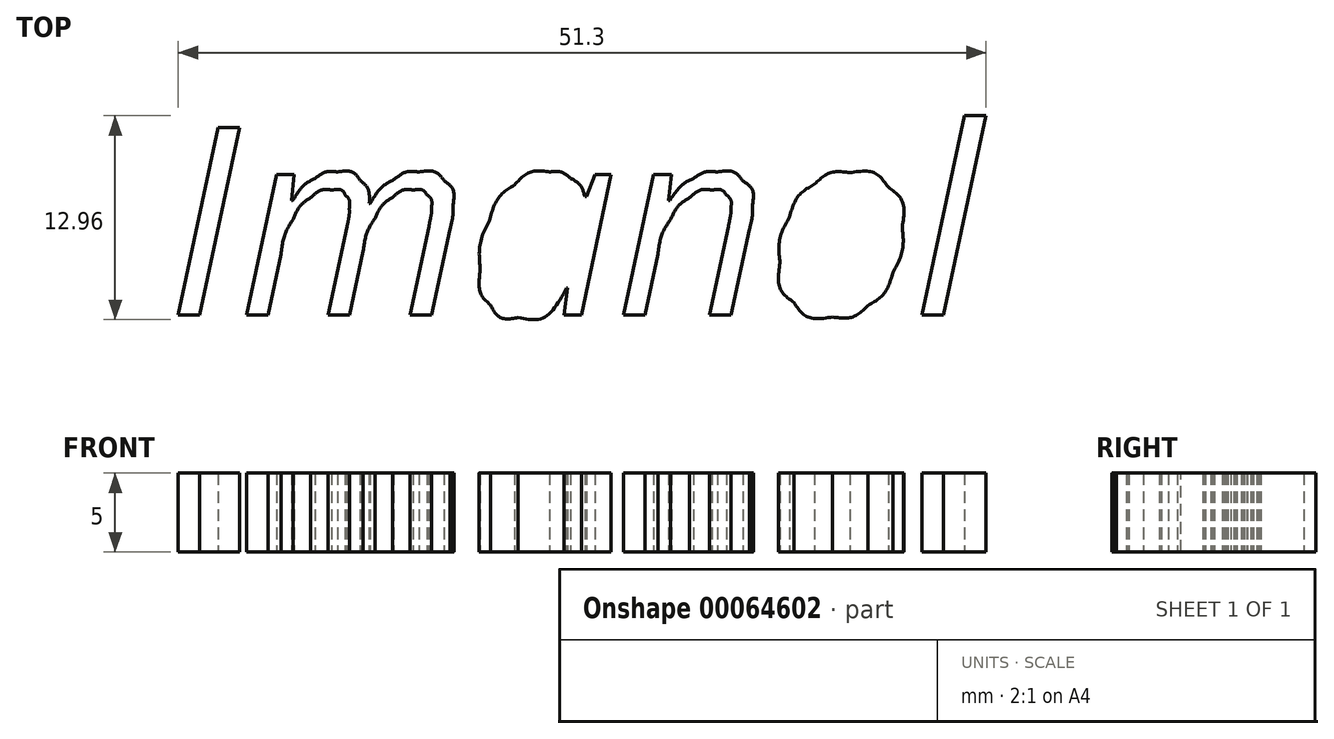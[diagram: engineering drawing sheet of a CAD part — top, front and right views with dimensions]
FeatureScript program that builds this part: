
annotation { "Feature Type Name" : "Feature", "Feature Type Description" : "" }
export const myFeature = defineFeature(function(context is Context, id is Id, definition is map)
    precondition{}
    {
        {
            var Q0;
            Q0=qCreatedBy(makeId("Top.planeOp"),FACE);
            var sketch = newSketch(context, id + "F0", { "sketchPlane" : qUnion([Q0])});
            skLineSegment(sketch, "E0.rect.bottom", {"start": v(30, 12.5) * mm, "end": v(-30, 12.5) * mm});
            skLineSegment(sketch, "E0.rect.top", {"start": v(30, -12.5) * mm, "end": v(-30, -12.5) * mm});
            skLineSegment(sketch, "E0.rect.left", {"start": v(30, 12.5) * mm, "end": v(30, -12.5) * mm});
            skPoint(sketch, "E0.rect.middle", {"position": v(0, 0) * mm});
            skArc(sketch, "E1", {"start": v(-30, 12.5) * mm, "mid": v(-42.5, 0) * mm, "end": v(-30, -12.5) * mm});
            skCircle(sketch, "E2", {"center": v(-35.34, 0) * mm, "radius": 2.5 * mm});
            skSolve(sketch);
        }
        {
            var Q0;
            Q0 = qSketchRegion(id + "F0", true);
            extrude(context, id + "F1", {"entities" : qUnion([Q0]), "depth" : 3 * mm});
        }
        {
            var Q0;
            Q0=makeQuery(id+"F1.opExtrude","CAP_FACE",FACE,{"disambiguationData":[OSD([sQuery(id+"F0.wireOp",EDGE,"E0.rect.bottom"),sQuery(id+"F0.wireOp",EDGE,"E0.rect.top"),sQuery(id+"F0.wireOp",EDGE,"E0.rect.left"),sQuery(id+"F0.wireOp",EDGE,"E1"),sQuery(id+"F0.wireOp",EDGE,"E2")])],"isStart":false});
            var sketch = newSketch(context, id + "F2", { "sketchPlane" : qUnion([Q0])});
            skLineSegment(sketch, "E3.0.0", {"start": v(-23.45, 7.78) * mm, "end": v(-25.98, -4.12) * mm});
            skLineSegment(sketch, "E3.0.1", {"start": v(-25.98, -4.12) * mm, "end": v(-24.61, -4.12) * mm});
            skLineSegment(sketch, "E3.0.2", {"start": v(-24.61, -4.12) * mm, "end": v(-22.08, 7.78) * mm});
            skLineSegment(sketch, "E3.0.3", {"start": v(-22.08, 7.78) * mm, "end": v(-23.45, 7.78) * mm});
            skLineSegment(sketch, "E4.0.0", {"start": v(-15.26, 1.51) * mm, "end": v(-16.47, -4.12) * mm});
            skLineSegment(sketch, "E4.0.1", {"start": v(-16.47, -4.12) * mm, "end": v(-15.1, -4.12) * mm});
            skLineSegment(sketch, "E4.0.2", {"start": v(-15.1, -4.12) * mm, "end": v(-14.23, -0.04) * mm});
            skFitSpline(sketch, "E4.0.3", {"points": [v(-14.23, -0.05) * mm, v(-13.98, 1.14) * mm, v(-13.5, 2) * mm]});
            skFitSpline(sketch, "E4.0.4", {"points": [v(-13.5, 2) * mm, v(-13, 2.87) * mm, v(-12.37, 3.34) * mm]});
            skFitSpline(sketch, "E4.0.5", {"points": [v(-12.37, 3.34) * mm, v(-11.72, 3.81) * mm, v(-11.06, 3.81) * mm]});
            skFitSpline(sketch, "E4.0.6", {"points": [v(-11.06, 3.81) * mm, v(-10.46, 3.81) * mm, v(-10.18, 3.5) * mm]});
            skFitSpline(sketch, "E4.0.7", {"points": [v(-10.18, 3.5) * mm, v(-9.9, 3.2) * mm, v(-9.9, 2.7) * mm]});
            skFitSpline(sketch, "E4.0.8", {"points": [v(-9.9, 2.7) * mm, v(-9.9, 2.36) * mm, v(-10.06, 1.51) * mm]});
            skLineSegment(sketch, "E4.0.9", {"start": v(-10.06, 1.51) * mm, "end": v(-11.27, -4.12) * mm});
            skLineSegment(sketch, "E4.0.10", {"start": v(-11.27, -4.12) * mm, "end": v(-9.88, -4.12) * mm});
            skLineSegment(sketch, "E4.0.11", {"start": v(-9.88, -4.12) * mm, "end": v(-8.71, 1.35) * mm});
            skFitSpline(sketch, "E4.0.12", {"points": [v(-8.71, 1.35) * mm, v(-8.53, 2.24) * mm, v(-8.53, 2.8) * mm]});
            skFitSpline(sketch, "E4.0.13", {"points": [v(-8.53, 2.8) * mm, v(-8.53, 3.85) * mm, v(-9.1, 4.4) * mm]});
            skFitSpline(sketch, "E4.0.14", {"points": [v(-9.1, 4.4) * mm, v(-9.66, 4.96) * mm, v(-10.7, 4.96) * mm]});
            skFitSpline(sketch, "E4.0.15", {"points": [v(-10.7, 4.96) * mm, v(-11.5, 4.96) * mm, v(-12.3, 4.47) * mm]});
            skFitSpline(sketch, "E4.0.16", {"points": [v(-12.3, 4.47) * mm, v(-13.08, 3.97) * mm, v(-13.78, 2.96) * mm]});
            skLineSegment(sketch, "E4.0.17", {"start": v(-13.78, 2.96) * mm, "end": v(-13.85, 2.96) * mm});
            skFitSpline(sketch, "E4.0.18", {"points": [v(-13.85, 2.96) * mm, v(-13.94, 3.9) * mm, v(-14.43, 4.43) * mm]});
            skFitSpline(sketch, "E4.0.19", {"points": [v(-14.43, 4.43) * mm, v(-14.93, 4.96) * mm, v(-15.85, 4.96) * mm]});
            skFitSpline(sketch, "E4.0.20", {"points": [v(-15.85, 4.96) * mm, v(-16.6, 4.96) * mm, v(-17.3, 4.54) * mm]});
            skFitSpline(sketch, "E4.0.21", {"points": [v(-17.3, 4.54) * mm, v(-18, 4.11) * mm, v(-18.71, 3.15) * mm]});
            skLineSegment(sketch, "E4.0.22", {"start": v(-18.71, 3.15) * mm, "end": v(-18.8, 3.15) * mm});
            skLineSegment(sketch, "E4.0.23", {"start": v(-18.8, 3.15) * mm, "end": v(-18.62, 4.8) * mm});
            skLineSegment(sketch, "E4.0.24", {"start": v(-18.62, 4.8) * mm, "end": v(-19.75, 4.8) * mm});
            skLineSegment(sketch, "E4.0.25", {"start": v(-19.75, 4.8) * mm, "end": v(-21.65, -4.12) * mm});
            skLineSegment(sketch, "E4.0.26", {"start": v(-21.65, -4.12) * mm, "end": v(-20.29, -4.12) * mm});
            skLineSegment(sketch, "E4.0.27", {"start": v(-20.29, -4.12) * mm, "end": v(-19.46, -0.26) * mm});
            skFitSpline(sketch, "E4.0.28", {"points": [v(-19.46, -0.26) * mm, v(-19.2, 1.02) * mm, v(-18.7, 1.93) * mm]});
            skFitSpline(sketch, "E4.0.29", {"points": [v(-18.7, 1.93) * mm, v(-18.21, 2.84) * mm, v(-17.56, 3.32) * mm]});
            skFitSpline(sketch, "E4.0.30", {"points": [v(-17.56, 3.32) * mm, v(-16.92, 3.81) * mm, v(-16.23, 3.81) * mm]});
            skFitSpline(sketch, "E4.0.31", {"points": [v(-16.23, 3.81) * mm, v(-15.62, 3.81) * mm, v(-15.37, 3.5) * mm]});
            skFitSpline(sketch, "E4.0.32", {"points": [v(-15.37, 3.5) * mm, v(-15.12, 3.18) * mm, v(-15.12, 2.6) * mm]});
            skFitSpline(sketch, "E4.0.33", {"points": [v(-15.12, 2.6) * mm, v(-15.12, 2.27) * mm, v(-15.26, 1.51) * mm]});
            skFitSpline(sketch, "E5.0.0", {"points": [v(-1.06, 4.56) * mm, v(-1.65, 4.96) * mm, v(-2.4, 4.96) * mm]});
            skFitSpline(sketch, "E5.0.1", {"points": [v(-2.4, 4.96) * mm, v(-3.61, 4.96) * mm, v(-4.63, 4.14) * mm]});
            skFitSpline(sketch, "E5.0.2", {"points": [v(-4.63, 4.14) * mm, v(-5.64, 3.32) * mm, v(-6.22, 1.87) * mm]});
            skFitSpline(sketch, "E5.0.3", {"points": [v(-6.22, 1.87) * mm, v(-6.8, 0.42) * mm, v(-6.8, -1.27) * mm]});
            skFitSpline(sketch, "E5.0.4", {"points": [v(-6.8, -1.27) * mm, v(-6.8, -2.67) * mm, v(-6.16, -3.48) * mm]});
            skFitSpline(sketch, "E5.0.5", {"points": [v(-6.16, -3.48) * mm, v(-5.51, -4.29) * mm, v(-4.38, -4.29) * mm]});
            skFitSpline(sketch, "E5.0.6", {"points": [v(-4.38, -4.29) * mm, v(-2.77, -4.29) * mm, v(-1.31, -2.42) * mm]});
            skLineSegment(sketch, "E5.0.7", {"start": v(-1.31, -2.42) * mm, "end": v(-1.25, -2.42) * mm});
            skLineSegment(sketch, "E5.0.8", {"start": v(-1.25, -2.42) * mm, "end": v(-1.46, -4.12) * mm});
            skLineSegment(sketch, "E5.0.9", {"start": v(-1.46, -4.12) * mm, "end": v(-0.38, -4.12) * mm});
            skLineSegment(sketch, "E5.0.10", {"start": v(-0.38, -4.12) * mm, "end": v(1.52, 4.8) * mm});
            skLineSegment(sketch, "E5.0.11", {"start": v(1.52, 4.8) * mm, "end": v(0.48, 4.8) * mm});
            skLineSegment(sketch, "E5.0.12", {"start": v(0.48, 4.8) * mm, "end": v(-0.06, 3.4) * mm});
            skLineSegment(sketch, "E5.0.13", {"start": v(-0.06, 3.4) * mm, "end": v(-0.15, 3.4) * mm});
            skFitSpline(sketch, "E5.0.14", {"points": [v(-0.15, 3.4) * mm, v(-0.48, 4.15) * mm, v(-1.06, 4.56) * mm]});
            skLineSegment(sketch, "E6.0.0", {"start": v(8.96, 1.51) * mm, "end": v(7.75, -4.12) * mm});
            skLineSegment(sketch, "E6.0.1", {"start": v(7.75, -4.12) * mm, "end": v(9.13, -4.12) * mm});
            skLineSegment(sketch, "E6.0.2", {"start": v(9.13, -4.12) * mm, "end": v(10.3, 1.35) * mm});
            skFitSpline(sketch, "E6.0.3", {"points": [v(10.3, 1.35) * mm, v(10.49, 2.17) * mm, v(10.49, 2.81) * mm]});
            skFitSpline(sketch, "E6.0.4", {"points": [v(10.49, 2.81) * mm, v(10.49, 3.83) * mm, v(9.89, 4.4) * mm]});
            skFitSpline(sketch, "E6.0.5", {"points": [v(9.89, 4.4) * mm, v(9.29, 4.96) * mm, v(8.26, 4.96) * mm]});
            skFitSpline(sketch, "E6.0.6", {"points": [v(8.26, 4.96) * mm, v(7.47, 4.96) * mm, v(6.75, 4.55) * mm]});
            skFitSpline(sketch, "E6.0.7", {"points": [v(6.75, 4.55) * mm, v(6.02, 4.14) * mm, v(5.24, 3.15) * mm]});
            skLineSegment(sketch, "E6.0.8", {"start": v(5.24, 3.15) * mm, "end": v(5.15, 3.15) * mm});
            skLineSegment(sketch, "E6.0.9", {"start": v(5.15, 3.15) * mm, "end": v(5.33, 4.8) * mm});
            skLineSegment(sketch, "E6.0.10", {"start": v(5.33, 4.8) * mm, "end": v(4.2, 4.8) * mm});
            skLineSegment(sketch, "E6.0.11", {"start": v(4.2, 4.8) * mm, "end": v(2.3, -4.12) * mm});
            skLineSegment(sketch, "E6.0.12", {"start": v(2.3, -4.12) * mm, "end": v(3.66, -4.12) * mm});
            skLineSegment(sketch, "E6.0.13", {"start": v(3.66, -4.12) * mm, "end": v(4.49, -0.26) * mm});
            skFitSpline(sketch, "E6.0.14", {"points": [v(4.49, -0.26) * mm, v(4.76, 1.03) * mm, v(5.28, 1.93) * mm]});
            skFitSpline(sketch, "E6.0.15", {"points": [v(5.28, 1.93) * mm, v(5.8, 2.84) * mm, v(6.5, 3.32) * mm]});
            skFitSpline(sketch, "E6.0.16", {"points": [v(6.5, 3.32) * mm, v(7.18, 3.81) * mm, v(7.9, 3.81) * mm]});
            skFitSpline(sketch, "E6.0.17", {"points": [v(7.9, 3.81) * mm, v(8.54, 3.81) * mm, v(8.83, 3.5) * mm]});
            skFitSpline(sketch, "E6.0.18", {"points": [v(8.83, 3.5) * mm, v(9.12, 3.2) * mm, v(9.12, 2.68) * mm]});
            skFitSpline(sketch, "E6.0.19", {"points": [v(9.12, 2.68) * mm, v(9.12, 2.36) * mm, v(8.96, 1.51) * mm]});
            skFitSpline(sketch, "E7.0.0", {"points": [v(19.11, 4) * mm, v(18.22, 4.91) * mm, v(16.67, 4.91) * mm]});
            skFitSpline(sketch, "E7.0.1", {"points": [v(16.67, 4.91) * mm, v(15.44, 4.91) * mm, v(14.43, 4.18) * mm]});
            skFitSpline(sketch, "E7.0.2", {"points": [v(14.43, 4.18) * mm, v(13.43, 3.45) * mm, v(12.83, 2.1) * mm]});
            skFitSpline(sketch, "E7.0.3", {"points": [v(12.83, 2.1) * mm, v(12.24, 0.73) * mm, v(12.24, -0.82) * mm]});
            skFitSpline(sketch, "E7.0.4", {"points": [v(12.24, -0.82) * mm, v(12.24, -2.41) * mm, v(13.12, -3.33) * mm]});
            skFitSpline(sketch, "E7.0.5", {"points": [v(13.12, -3.33) * mm, v(14.01, -4.25) * mm, v(15.57, -4.25) * mm]});
            skFitSpline(sketch, "E7.0.6", {"points": [v(15.57, -4.25) * mm, v(16.83, -4.25) * mm, v(17.84, -3.51) * mm]});
            skFitSpline(sketch, "E7.0.7", {"points": [v(17.84, -3.51) * mm, v(18.84, -2.77) * mm, v(19.42, -1.41) * mm]});
            skFitSpline(sketch, "E7.0.8", {"points": [v(19.42, -1.41) * mm, v(20, -0.05) * mm, v(20, 1.48) * mm]});
            skFitSpline(sketch, "E7.0.9", {"points": [v(20, 1.48) * mm, v(20, 3.08) * mm, v(19.11, 4) * mm]});
            skLineSegment(sketch, "E8.0.0", {"start": v(21.25, -4.12) * mm, "end": v(22.62, -4.12) * mm});
            skLineSegment(sketch, "E8.0.1", {"start": v(22.62, -4.12) * mm, "end": v(25.32, 8.54) * mm});
            skLineSegment(sketch, "E8.0.2", {"start": v(25.32, 8.54) * mm, "end": v(23.96, 8.54) * mm});
            skLineSegment(sketch, "E8.0.3", {"start": v(23.96, 8.54) * mm, "end": v(21.25, -4.12) * mm});
            skLineSegment(sketch, "E9.rect.bottom", {"start": v(42.93, 26.44) * mm, "end": v(-52.19, 26.44) * mm});
            skLineSegment(sketch, "E9.rect.top", {"start": v(42.93, -31.29) * mm, "end": v(-52.19, -31.29) * mm});
            skLineSegment(sketch, "E9.rect.left", {"start": v(42.93, 26.44) * mm, "end": v(42.93, -31.29) * mm});
            skLineSegment(sketch, "E9.rect.right", {"start": v(-52.19, 26.44) * mm, "end": v(-52.19, -31.29) * mm});
            skPoint(sketch, "E9.rect.middle", {"position": v(-4.63, -2.42) * mm});
            skSolve(sketch);
        }
        {
            var Q0;
            Q0=makeQuery(id+"F2.imprint","IMPRINT",FACE,{"disambiguationData":[TD([[makeQuery(id+"F2.imprint","IMPRINT",EDGE,{"derivedFrom":sQuery(id+"F2.wireOp",EDGE,"E3.0.0")}),1.0]])]});
            var Q1;
            Q1=makeQuery(id+"F2.imprint","IMPRINT",FACE,{"disambiguationData":[TD([[makeQuery(id+"F2.imprint","IMPRINT",EDGE,{"derivedFrom":sQuery(id+"F2.wireOp",EDGE,"E4.0.0")}),1.0]])]});
            var Q2;
            Q2=makeQuery(id+"F2.imprint","IMPRINT",FACE,{"disambiguationData":[TD([[makeQuery(id+"F2.imprint","IMPRINT",EDGE,{"derivedFrom":sQuery(id+"F2.wireOp",EDGE,"E5.0.0")}),1.0]])]});
            var Q3;
            Q3=makeQuery(id+"F2.imprint","IMPRINT",FACE,{"disambiguationData":[TD([[makeQuery(id+"F2.imprint","IMPRINT",EDGE,{"derivedFrom":sQuery(id+"F2.wireOp",EDGE,"E6.0.0")}),1.0]])]});
            var Q4;
            Q4=makeQuery(id+"F2.imprint","IMPRINT",FACE,{"disambiguationData":[TD([[makeQuery(id+"F2.imprint","IMPRINT",EDGE,{"derivedFrom":sQuery(id+"F2.wireOp",EDGE,"E7.0.0")}),1.0]])]});
            var Q5;
            Q5=makeQuery(id+"F2.imprint","IMPRINT",FACE,{"disambiguationData":[TD([[makeQuery(id+"F2.imprint","IMPRINT",EDGE,{"derivedFrom":sQuery(id+"F2.wireOp",EDGE,"E8.0.0")}),1.0]])]});
            extrude(context, id + "F3", {"entities" : qUnion([Q0, Q1, Q2, Q3, Q4, Q5]), "operationType" : NewBodyOperationType.REMOVE, "oppositeDirection" : true, "depth" : 2 * mm});
        }
        {
            var Q0;
            Q0 = qSketchRegion(id + "F2", true);
            extrude(context, id + "F4", {"entities" : qUnion([Q0]), "operationType" : NewBodyOperationType.REMOVE, "oppositeDirection" : true, "depth" : 25 * mm});
        }
        {
            var Q0;
            Q0=makeQuery(id+"F3.boolean.opBoolean","COPY",FACE,{"derivedFrom":makeQuery(id+"F3.opExtrude","CAP_FACE",FACE,{"disambiguationData":[OSD([sQuery(id+"F2.wireOp",EDGE,"E5.0.0"),sQuery(id+"F2.wireOp",EDGE,"E5.0.1"),sQuery(id+"F2.wireOp",EDGE,"E5.0.2"),sQuery(id+"F2.wireOp",EDGE,"E5.0.3"),sQuery(id+"F2.wireOp",EDGE,"E5.0.4"),sQuery(id+"F2.wireOp",EDGE,"E5.0.5"),sQuery(id+"F2.wireOp",EDGE,"E5.0.6"),sQuery(id+"F2.wireOp",EDGE,"E5.0.7"),sQuery(id+"F2.wireOp",EDGE,"E5.0.8"),sQuery(id+"F2.wireOp",EDGE,"E5.0.9"),sQuery(id+"F2.wireOp",EDGE,"E5.0.10"),sQuery(id+"F2.wireOp",EDGE,"E5.0.11"),sQuery(id+"F2.wireOp",EDGE,"E5.0.12"),sQuery(id+"F2.wireOp",EDGE,"E5.0.13"),sQuery(id+"F2.wireOp",EDGE,"E5.0.14")])],"isStart":false})});
            var sketch = newSketch(context, id + "F5", { "sketchPlane" : qUnion([Q0])});
            skLineSegment(sketch, "E10.0.0", {"start": v(-22.08, 7.78) * mm, "end": v(-23.45, 7.78) * mm});
            skLineSegment(sketch, "E10.0.1", {"start": v(-23.45, 7.78) * mm, "end": v(-25.98, -4.12) * mm});
            skLineSegment(sketch, "E10.0.2", {"start": v(-25.98, -4.12) * mm, "end": v(-24.61, -4.12) * mm});
            skLineSegment(sketch, "E10.0.3", {"start": v(-24.61, -4.12) * mm, "end": v(-22.08, 7.78) * mm});
            skFitSpline(sketch, "E11.0.0", {"points": [v(-15.12, 2.6) * mm, v(-15.12, 2.27) * mm, v(-15.26, 1.51) * mm]});
            skLineSegment(sketch, "E11.0.1", {"start": v(-15.26, 1.51) * mm, "end": v(-16.47, -4.12) * mm});
            skLineSegment(sketch, "E11.0.2", {"start": v(-16.47, -4.12) * mm, "end": v(-15.1, -4.12) * mm});
            skLineSegment(sketch, "E11.0.3", {"start": v(-15.1, -4.12) * mm, "end": v(-14.23, -0.04) * mm});
            skFitSpline(sketch, "E11.0.4", {"points": [v(-14.23, -0.05) * mm, v(-13.98, 1.14) * mm, v(-13.5, 2) * mm]});
            skFitSpline(sketch, "E11.0.5", {"points": [v(-13.5, 2) * mm, v(-13, 2.87) * mm, v(-12.37, 3.34) * mm]});
            skFitSpline(sketch, "E11.0.6", {"points": [v(-12.37, 3.34) * mm, v(-11.72, 3.81) * mm, v(-11.06, 3.81) * mm]});
            skFitSpline(sketch, "E11.0.7", {"points": [v(-11.06, 3.81) * mm, v(-10.46, 3.81) * mm, v(-10.18, 3.5) * mm]});
            skFitSpline(sketch, "E11.0.8", {"points": [v(-10.18, 3.5) * mm, v(-9.9, 3.2) * mm, v(-9.9, 2.7) * mm]});
            skFitSpline(sketch, "E11.0.9", {"points": [v(-9.9, 2.7) * mm, v(-9.9, 2.36) * mm, v(-10.06, 1.51) * mm]});
            skLineSegment(sketch, "E11.0.10", {"start": v(-10.06, 1.51) * mm, "end": v(-11.27, -4.12) * mm});
            skLineSegment(sketch, "E11.0.11", {"start": v(-11.27, -4.12) * mm, "end": v(-9.88, -4.12) * mm});
            skLineSegment(sketch, "E11.0.12", {"start": v(-9.88, -4.12) * mm, "end": v(-8.71, 1.35) * mm});
            skFitSpline(sketch, "E11.0.13", {"points": [v(-8.71, 1.35) * mm, v(-8.53, 2.24) * mm, v(-8.53, 2.8) * mm]});
            skFitSpline(sketch, "E11.0.14", {"points": [v(-8.53, 2.8) * mm, v(-8.53, 3.85) * mm, v(-9.1, 4.4) * mm]});
            skFitSpline(sketch, "E11.0.15", {"points": [v(-9.1, 4.4) * mm, v(-9.66, 4.96) * mm, v(-10.7, 4.96) * mm]});
            skFitSpline(sketch, "E11.0.16", {"points": [v(-10.7, 4.96) * mm, v(-11.5, 4.96) * mm, v(-12.3, 4.47) * mm]});
            skFitSpline(sketch, "E11.0.17", {"points": [v(-12.3, 4.47) * mm, v(-13.08, 3.97) * mm, v(-13.78, 2.96) * mm]});
            skLineSegment(sketch, "E11.0.18", {"start": v(-13.78, 2.96) * mm, "end": v(-13.85, 2.96) * mm});
            skFitSpline(sketch, "E11.0.19", {"points": [v(-13.85, 2.96) * mm, v(-13.94, 3.9) * mm, v(-14.43, 4.43) * mm]});
            skFitSpline(sketch, "E11.0.20", {"points": [v(-14.43, 4.43) * mm, v(-14.93, 4.96) * mm, v(-15.85, 4.96) * mm]});
            skFitSpline(sketch, "E11.0.21", {"points": [v(-15.85, 4.96) * mm, v(-16.6, 4.96) * mm, v(-17.3, 4.54) * mm]});
            skFitSpline(sketch, "E11.0.22", {"points": [v(-17.3, 4.54) * mm, v(-18, 4.11) * mm, v(-18.71, 3.15) * mm]});
            skLineSegment(sketch, "E11.0.23", {"start": v(-18.71, 3.15) * mm, "end": v(-18.8, 3.15) * mm});
            skLineSegment(sketch, "E11.0.24", {"start": v(-18.8, 3.15) * mm, "end": v(-18.62, 4.8) * mm});
            skLineSegment(sketch, "E11.0.25", {"start": v(-18.62, 4.8) * mm, "end": v(-19.75, 4.8) * mm});
            skLineSegment(sketch, "E11.0.26", {"start": v(-19.75, 4.8) * mm, "end": v(-21.65, -4.12) * mm});
            skLineSegment(sketch, "E11.0.27", {"start": v(-21.65, -4.12) * mm, "end": v(-20.29, -4.12) * mm});
            skLineSegment(sketch, "E11.0.28", {"start": v(-20.29, -4.12) * mm, "end": v(-19.46, -0.26) * mm});
            skFitSpline(sketch, "E11.0.29", {"points": [v(-19.46, -0.26) * mm, v(-19.2, 1.02) * mm, v(-18.7, 1.93) * mm]});
            skFitSpline(sketch, "E11.0.30", {"points": [v(-18.7, 1.93) * mm, v(-18.21, 2.84) * mm, v(-17.56, 3.32) * mm]});
            skFitSpline(sketch, "E11.0.31", {"points": [v(-17.56, 3.32) * mm, v(-16.92, 3.81) * mm, v(-16.23, 3.81) * mm]});
            skFitSpline(sketch, "E11.0.32", {"points": [v(-16.23, 3.81) * mm, v(-15.62, 3.81) * mm, v(-15.37, 3.5) * mm]});
            skFitSpline(sketch, "E11.0.33", {"points": [v(-15.37, 3.5) * mm, v(-15.12, 3.18) * mm, v(-15.12, 2.6) * mm]});
            skFitSpline(sketch, "E12.0.0", {"points": [v(-0.15, 3.4) * mm, v(-0.48, 4.15) * mm, v(-1.06, 4.56) * mm]});
            skFitSpline(sketch, "E12.0.1", {"points": [v(-1.06, 4.56) * mm, v(-1.65, 4.96) * mm, v(-2.4, 4.96) * mm]});
            skFitSpline(sketch, "E12.0.2", {"points": [v(-2.4, 4.96) * mm, v(-3.61, 4.96) * mm, v(-4.63, 4.14) * mm]});
            skFitSpline(sketch, "E12.0.3", {"points": [v(-4.63, 4.14) * mm, v(-5.64, 3.32) * mm, v(-6.22, 1.87) * mm]});
            skFitSpline(sketch, "E12.0.4", {"points": [v(-6.22, 1.87) * mm, v(-6.8, 0.42) * mm, v(-6.8, -1.27) * mm]});
            skFitSpline(sketch, "E12.0.5", {"points": [v(-6.8, -1.27) * mm, v(-6.8, -2.67) * mm, v(-6.16, -3.48) * mm]});
            skFitSpline(sketch, "E12.0.6", {"points": [v(-6.16, -3.48) * mm, v(-5.51, -4.29) * mm, v(-4.38, -4.29) * mm]});
            skFitSpline(sketch, "E12.0.7", {"points": [v(-4.38, -4.29) * mm, v(-2.77, -4.29) * mm, v(-1.31, -2.42) * mm]});
            skLineSegment(sketch, "E12.0.8", {"start": v(-1.31, -2.42) * mm, "end": v(-1.25, -2.42) * mm});
            skLineSegment(sketch, "E12.0.9", {"start": v(-1.25, -2.42) * mm, "end": v(-1.46, -4.12) * mm});
            skLineSegment(sketch, "E12.0.10", {"start": v(-1.46, -4.12) * mm, "end": v(-0.38, -4.12) * mm});
            skLineSegment(sketch, "E12.0.11", {"start": v(-0.38, -4.12) * mm, "end": v(1.52, 4.8) * mm});
            skLineSegment(sketch, "E12.0.12", {"start": v(1.52, 4.8) * mm, "end": v(0.48, 4.8) * mm});
            skLineSegment(sketch, "E12.0.13", {"start": v(0.48, 4.8) * mm, "end": v(-0.06, 3.4) * mm});
            skLineSegment(sketch, "E12.0.14", {"start": v(-0.06, 3.4) * mm, "end": v(-0.15, 3.4) * mm});
            skLineSegment(sketch, "E13.0", {"start": v(4.2, 4.8) * mm, "end": v(2.3, -4.12) * mm});
            skFitSpline(sketch, "E14.0", {"points": [v(4.49, -0.26) * mm, v(4.76, 1.03) * mm, v(5.28, 1.93) * mm]});
            skFitSpline(sketch, "E15.0.0", {"points": [v(20, 1.48) * mm, v(20, 3.08) * mm, v(19.11, 4) * mm]});
            skFitSpline(sketch, "E15.0.1", {"points": [v(19.11, 4) * mm, v(18.22, 4.91) * mm, v(16.67, 4.91) * mm]});
            skFitSpline(sketch, "E15.0.2", {"points": [v(16.67, 4.91) * mm, v(15.44, 4.91) * mm, v(14.43, 4.18) * mm]});
            skFitSpline(sketch, "E15.0.3", {"points": [v(14.43, 4.18) * mm, v(13.43, 3.45) * mm, v(12.83, 2.1) * mm]});
            skFitSpline(sketch, "E15.0.4", {"points": [v(12.83, 2.1) * mm, v(12.24, 0.73) * mm, v(12.24, -0.82) * mm]});
            skFitSpline(sketch, "E15.0.5", {"points": [v(12.24, -0.82) * mm, v(12.24, -2.41) * mm, v(13.12, -3.33) * mm]});
            skFitSpline(sketch, "E15.0.6", {"points": [v(13.12, -3.33) * mm, v(14.01, -4.25) * mm, v(15.57, -4.25) * mm]});
            skFitSpline(sketch, "E15.0.7", {"points": [v(15.57, -4.25) * mm, v(16.83, -4.25) * mm, v(17.84, -3.51) * mm]});
            skFitSpline(sketch, "E15.0.8", {"points": [v(17.84, -3.51) * mm, v(18.84, -2.77) * mm, v(19.42, -1.41) * mm]});
            skFitSpline(sketch, "E15.0.9", {"points": [v(19.42, -1.41) * mm, v(20, -0.05) * mm, v(20, 1.48) * mm]});
            skFitSpline(sketch, "E16.0.0", {"points": [v(9.12, 2.68) * mm, v(9.12, 2.36) * mm, v(8.96, 1.51) * mm]});
            skLineSegment(sketch, "E16.0.1", {"start": v(8.96, 1.51) * mm, "end": v(7.75, -4.12) * mm});
            skLineSegment(sketch, "E16.0.2", {"start": v(7.75, -4.12) * mm, "end": v(9.13, -4.12) * mm});
            skLineSegment(sketch, "E16.0.3", {"start": v(9.13, -4.12) * mm, "end": v(10.3, 1.35) * mm});
            skFitSpline(sketch, "E16.0.4", {"points": [v(10.3, 1.35) * mm, v(10.49, 2.17) * mm, v(10.49, 2.81) * mm]});
            skFitSpline(sketch, "E16.0.5", {"points": [v(10.49, 2.81) * mm, v(10.49, 3.83) * mm, v(9.89, 4.4) * mm]});
            skFitSpline(sketch, "E16.0.6", {"points": [v(9.89, 4.4) * mm, v(9.29, 4.96) * mm, v(8.26, 4.96) * mm]});
            skFitSpline(sketch, "E16.0.7", {"points": [v(8.26, 4.96) * mm, v(7.47, 4.96) * mm, v(6.75, 4.55) * mm]});
            skFitSpline(sketch, "E16.0.8", {"points": [v(6.75, 4.55) * mm, v(6.02, 4.14) * mm, v(5.24, 3.15) * mm]});
            skLineSegment(sketch, "E16.0.9", {"start": v(5.24, 3.15) * mm, "end": v(5.15, 3.15) * mm});
            skLineSegment(sketch, "E16.0.10", {"start": v(5.15, 3.15) * mm, "end": v(5.33, 4.8) * mm});
            skLineSegment(sketch, "E16.0.11", {"start": v(5.33, 4.8) * mm, "end": v(4.2, 4.8) * mm});
            skLineSegment(sketch, "E16.0.13", {"start": v(2.3, -4.12) * mm, "end": v(3.66, -4.12) * mm});
            skLineSegment(sketch, "E16.0.14", {"start": v(3.66, -4.12) * mm, "end": v(4.49, -0.26) * mm});
            skFitSpline(sketch, "E16.0.15", {"points": [v(4.49, -0.26) * mm, v(4.76, 1.03) * mm, v(5.28, 1.93) * mm]});
            skFitSpline(sketch, "E16.0.16", {"points": [v(5.28, 1.93) * mm, v(5.8, 2.84) * mm, v(6.5, 3.32) * mm]});
            skFitSpline(sketch, "E16.0.17", {"points": [v(6.5, 3.32) * mm, v(7.18, 3.81) * mm, v(7.9, 3.81) * mm]});
            skFitSpline(sketch, "E16.0.18", {"points": [v(7.9, 3.81) * mm, v(8.54, 3.81) * mm, v(8.83, 3.5) * mm]});
            skFitSpline(sketch, "E16.0.19", {"points": [v(8.83, 3.5) * mm, v(9.12, 3.2) * mm, v(9.12, 2.68) * mm]});
            skLineSegment(sketch, "E17.0.0", {"start": v(23.96, 8.54) * mm, "end": v(21.25, -4.12) * mm});
            skLineSegment(sketch, "E17.0.1", {"start": v(21.25, -4.12) * mm, "end": v(22.62, -4.12) * mm});
            skLineSegment(sketch, "E17.0.2", {"start": v(22.62, -4.12) * mm, "end": v(25.32, 8.54) * mm});
            skLineSegment(sketch, "E17.0.3", {"start": v(25.32, 8.54) * mm, "end": v(23.96, 8.54) * mm});
            skSolve(sketch);
        }
        {
            var Q0;
            Q0 = qSketchRegion(id + "F5", true);
            extrude(context, id + "F6", {"entities" : qUnion([Q0]), "depth" : 5 * mm});
        }
        {
            var Q0;
            Q0=makeQuery(id+"F4.boolean.opBoolean","SPLIT",FACE,{"disambiguationData":[TD([makeQuery(id+"F4.opExtrude","SWEPT_FACE",FACE,{"disambiguationData":[OSD([sQuery(id+"F2.wireOp",EDGE,"E7.0.0")])]})])],"derivedFrom":makeQuery(id+"F1.opExtrude","CAP_FACE",FACE,{"disambiguationData":[OSD([sQuery(id+"F0.wireOp",EDGE,"E0.rect.bottom"),sQuery(id+"F0.wireOp",EDGE,"E0.rect.top"),sQuery(id+"F0.wireOp",EDGE,"E0.rect.left"),sQuery(id+"F0.wireOp",EDGE,"E1"),sQuery(id+"F0.wireOp",EDGE,"E2")])],"isStart":true})});
            var sketch = newSketch(context, id + "F7", { "sketchPlane" : qUnion([Q0])});
            skLineSegment(sketch, "E18.rect.bottom", {"start": v(-36.92, -17.63) * mm, "end": v(30.14, -17.63) * mm});
            skLineSegment(sketch, "E18.rect.top", {"start": v(-36.92, 17.63) * mm, "end": v(30.14, 17.63) * mm});
            skLineSegment(sketch, "E18.rect.left", {"start": v(-36.92, -17.63) * mm, "end": v(-36.92, 17.63) * mm});
            skLineSegment(sketch, "E18.rect.right", {"start": v(30.14, -17.63) * mm, "end": v(30.14, 17.63) * mm});
            skPoint(sketch, "E18.rect.middle", {"position": v(-3.4, 0) * mm});
            skSolve(sketch);
        }
        {
            var Q0;
            Q0 = qSketchRegion(id + "F7", true);
            extrude(context, id + "F8", {"entities" : qUnion([Q0]), "operationType" : NewBodyOperationType.REMOVE, "oppositeDirection" : true, "depth" : 1 * mm});
        }
    });
